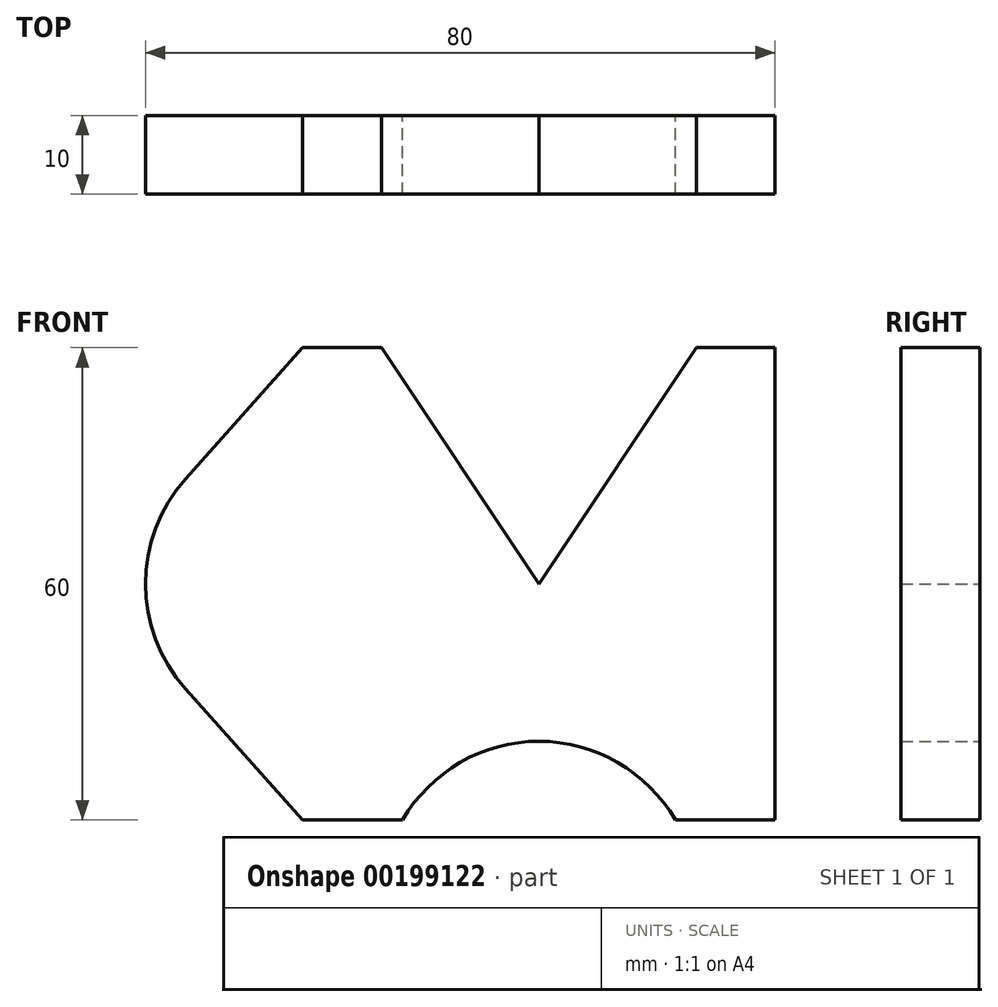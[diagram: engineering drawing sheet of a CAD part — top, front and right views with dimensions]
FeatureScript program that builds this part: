
annotation { "Feature Type Name" : "Feature", "Feature Type Description" : "" }
export const myFeature = defineFeature(function(context is Context, id is Id, definition is map)
    precondition{}
    {
        {
            var Q0;
            Q0=qCreatedBy(makeId("Front.planeOp"),FACE);
            var sketch = newSketch(context, id + "F0", { "sketchPlane" : qUnion([Q0])});
            skLineSegment(sketch, "E0", {"start": v(0, 0) * mm, "end": v(-20, 30) * mm});
            skLineSegment(sketch, "E1", {"start": v(-20, 30) * mm, "end": v(-30, 30) * mm});
            skLineSegment(sketch, "E2", {"start": v(0, 0) * mm, "end": v(20, 30) * mm});
            skLineSegment(sketch, "E3", {"start": v(20, 30) * mm, "end": v(30, 30) * mm});
            skLineSegment(sketch, "E4", {"start": v(30, 30) * mm, "end": v(30, -30) * mm});
            skLineSegment(sketch, "E5", {"start": v(30, -30) * mm, "end": v(17.32, -30) * mm});
            skLineSegment(sketch, "E6", {"start": v(-17.32, -30) * mm, "end": v(-30, -30) * mm});
            skArc(sketch, "E7", {"start": v(17.32, -30) * mm, "mid": v(0, -20) * mm, "end": v(-17.32, -30) * mm});
            skLineSegment(sketch, "E8", {"start": v(-30, 30) * mm, "end": v(-44.9, 13.33) * mm});
            skLineSegment(sketch, "E9", {"start": v(-30, -30) * mm, "end": v(-44.9, -13.33) * mm});
            skArc(sketch, "E10", {"start": v(-44.9, 13.33) * mm, "mid": v(-50, 0) * mm, "end": v(-44.9, -13.33) * mm});
            skLineSegment(sketch, "E11", {"start": v(-30, 30) * mm, "end": v(-30, -30) * mm, "construction": true});
            skSolve(sketch);
        }
        {
            var Q0;
            Q0 = qSketchRegion(id + "F0", true);
            extrude(context, id + "F1", {"entities" : qUnion([Q0]), "depth" : 10 * mm});
        }
    });
